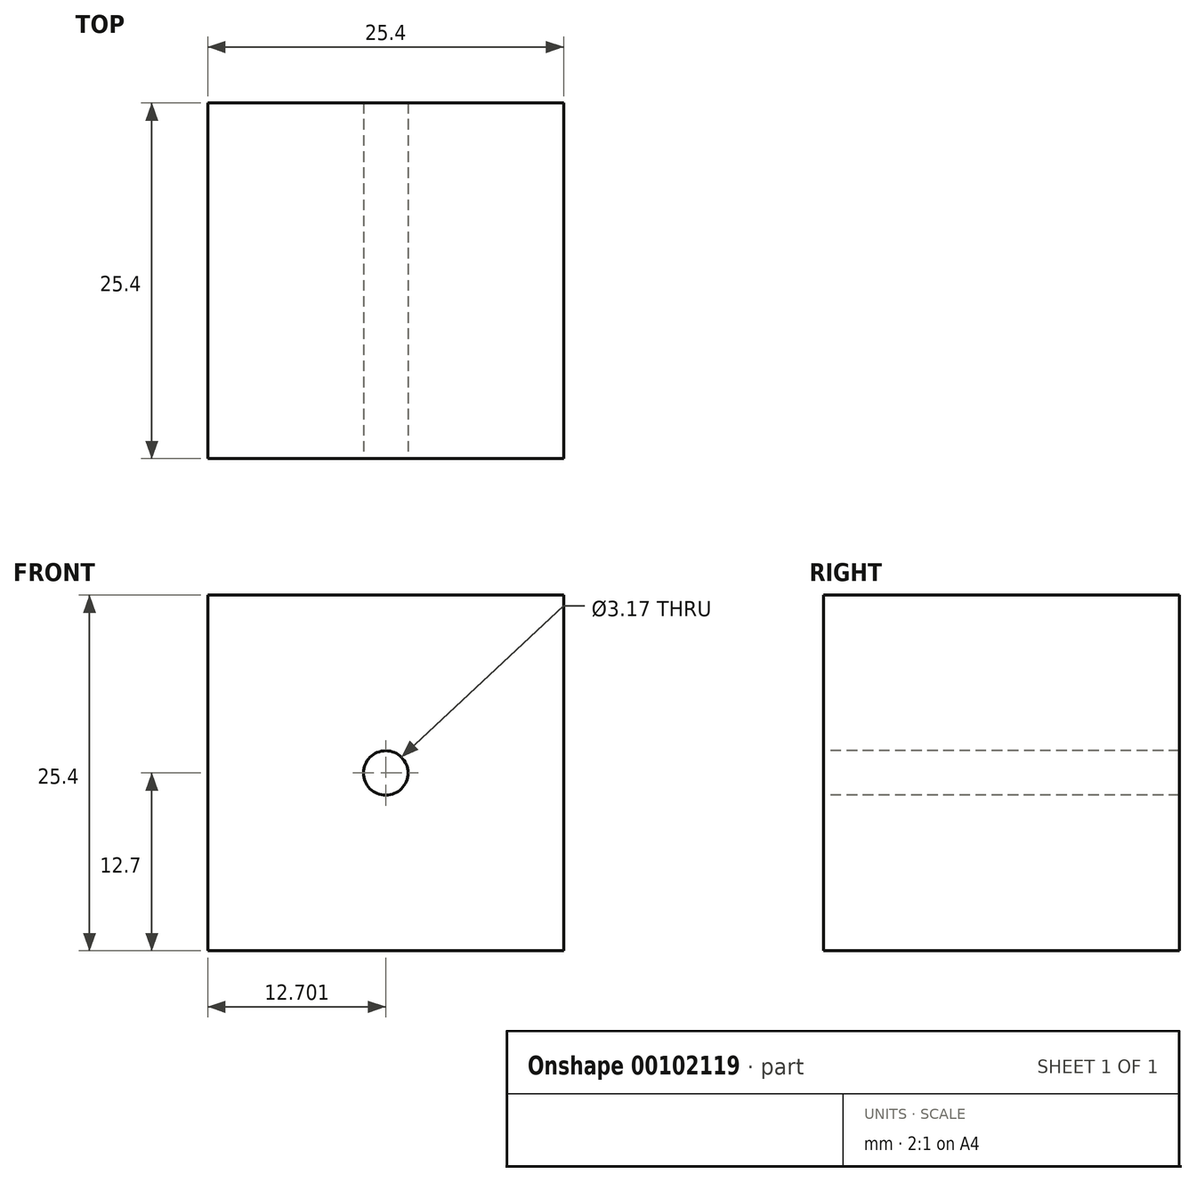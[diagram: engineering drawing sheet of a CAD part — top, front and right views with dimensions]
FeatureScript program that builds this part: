
annotation { "Feature Type Name" : "Feature", "Feature Type Description" : "" }
export const myFeature = defineFeature(function(context is Context, id is Id, definition is map)
    precondition{}
    {
        {
            var Q0;
            Q0=qCreatedBy(makeId("Top.planeOp"),FACE);
            var sketch = newSketch(context, id + "F0", { "sketchPlane" : qUnion([Q0])});
            skLineSegment(sketch, "E0.bottom", {"start": v(-10, 10.23) * mm, "end": v(15.4, 10.23) * mm});
            skLineSegment(sketch, "E0.top", {"start": v(-10, -15.17) * mm, "end": v(15.4, -15.17) * mm});
            skLineSegment(sketch, "E0.left", {"start": v(-10, 10.23) * mm, "end": v(-10, -15.17) * mm});
            skLineSegment(sketch, "E0.right", {"start": v(15.4, 10.23) * mm, "end": v(15.4, -15.17) * mm});
            skSolve(sketch);
        }
        {
            var Q0;
            Q0 = qSketchRegion(id + "F0", true);
            extrude(context, id + "F1", {"entities" : qUnion([Q0]), "depth" : 25.4 * mm});
        }
        {
            var Q0;
            Q0=makeQuery(id+"F1.opExtrude","SWEPT_FACE",FACE,{"disambiguationData":[OSD([sQuery(id+"F0.wireOp",EDGE,"E0.top")])]});
            var sketch = newSketch(context, id + "F2", { "sketchPlane" : qUnion([Q0])});
            skCircle(sketch, "E1", {"center": v(2.7, 12.7) * mm, "radius": 1.59 * mm});
            skPoint(sketch, "E1.centerSnap0", {"position": v(-10, 12.7) * mm});
            skPoint(sketch, "E1.centerSnap1", {"position": v(2.7, 0) * mm});
            skSolve(sketch);
        }
        {
            var Q0;
            Q0=makeQuery(id+"F2.imprint","IMPRINT",FACE,{"disambiguationData":[TD([[makeQuery(id+"F2.imprint","IMPRINT",EDGE,{"derivedFrom":sQuery(id+"F2.wireOp",EDGE,"E1")}),1.0]])]});
            extrude(context, id + "F3", {"entities" : qUnion([Q0]), "operationType" : NewBodyOperationType.REMOVE, "oppositeDirection" : true, "depth" : 25.4 * mm});
        }
    });
